# Revit family: Heating_Rheem_Tankpak_Series3_Internal_Standard_TPI01
name_source: partatom
category: Mechanical Equipment
units: mm (PartAtom-declared; Revit-internal decimal feet)

## family parameters
Always vertical = Yes
Cut with Voids When Loaded = No
OmniClass Number = 23.65.35.00
OmniClass Title = Heaters for Supplied Liquids
Part Type = Normal
Room Calculation Point = No
Round Connector Dimension = Use Diameter
Shared = No
Work Plane-Based = No

## types (2) — shared parameters
610340Type = StorageTank_Rheem_610Series_610340 : Standard
610430Type = StorageTank_Rheem_610Series_610430 : Standard
ApparentCurrent_ANZRS = 4 A
ApparentPower_ANZRS = 960 VA
CFWH Depth = 250 mm  [stored 0.82021 ft]
CFWH Height = 650 mm  [stored 2.13255 ft]
CFWH Top Height = 1600 mm  [stored 5.24934 ft]
CFWH Width = 350 mm  [stored 1.14829 ft]
ClearanceDepth = 600 mm
Controller Top Height = 850 mm  [stored 2.78871 ft]
Description = Rheem Tankpak Series 3 is the next phase in commercial water heating, combining the benefits of mains pressure and continuous flow water heating.

Rheem Tankpak Series 3 is supplied with the controller, pump, in line filter and water heater power supply factory assembled, requiring only connection of the storage tank on site.
ElectrialConnection = 1.8m 10A plug and lead
Frequency_ANZRS = 50 Hz
Manufacturer = Rheem
Model = Tankpak Series 3 - Internal
NumberOfPhases_ANZRS = 1
PowerFactor_ANZRS = 1
ProductCode_ANZRS = TPI01
URL = https://www.rheem.com.au
Voltage_ANZRS = 240 V
Width_ANZRS = 755 mm  [stored 2.47703 ft]
zero-valued in all types: Default Elevation

## per-type parameters (varying)
| type | Depth_ANZRS | Diameter_ANZRS | Height_ANZRS | Storage Tank Type |
| TPI01_610430 Tank | 935 mm | 685 mm  [stored 2.24738 ft] | 1840 mm  [stored 6.03675 ft] | StorageTank_Rheem_610Series_610430 : Standard |
| TPI01_610340 Tank | 890 mm  [stored 2.91995 ft] | 640 mm  [stored 2.09974 ft] | 1640 mm  [stored 5.38058 ft] | StorageTank_Rheem_610Series_610340 : Standard |

note: [stored X ft] marks values corroborated as IEEE doubles in the binary element streams (Revit-internal decimal feet)

## geometry (parser evidence)
native form markers: Sweep x19
no freeform markers — native parametric forms only
